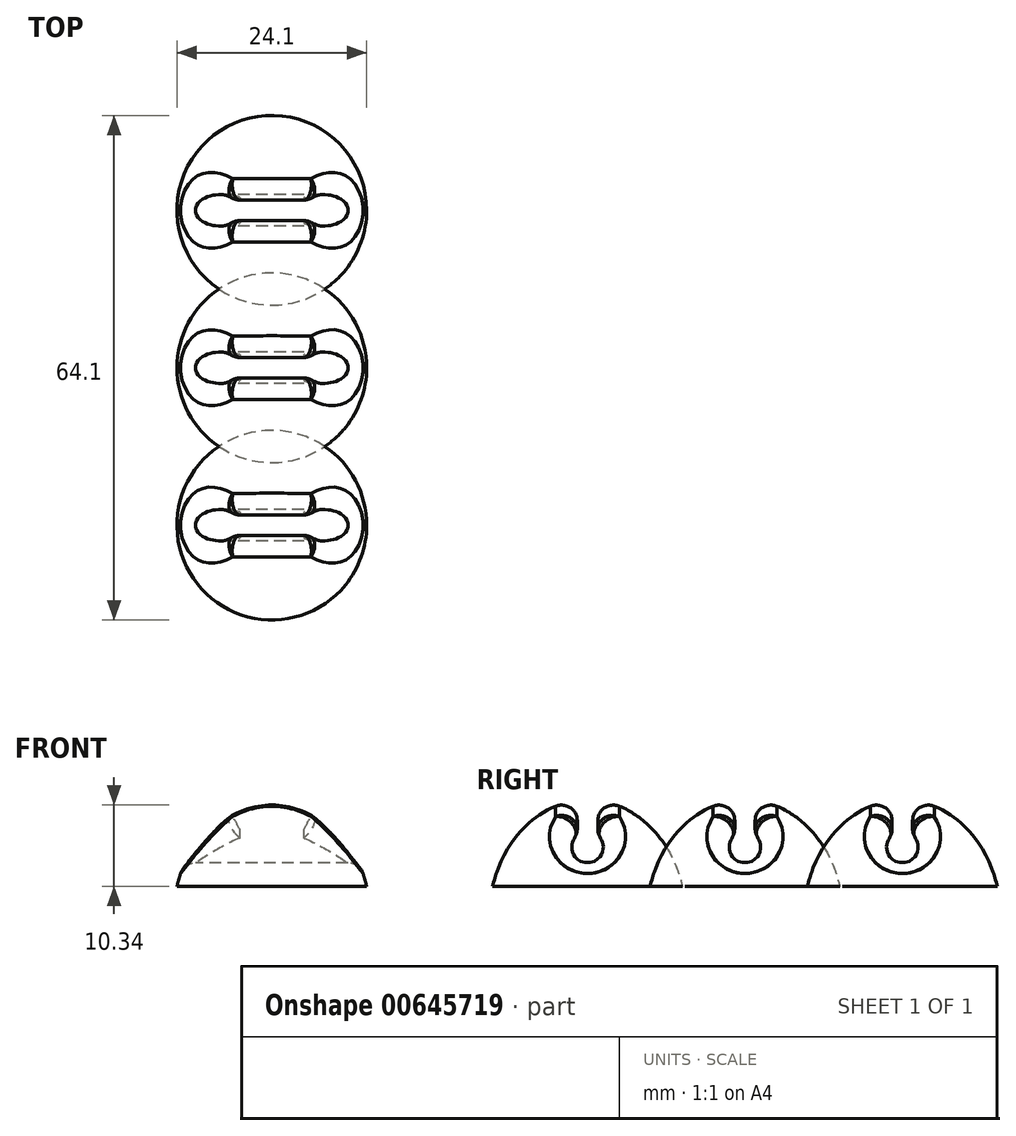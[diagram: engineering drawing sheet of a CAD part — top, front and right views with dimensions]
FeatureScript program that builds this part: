
annotation { "Feature Type Name" : "Feature", "Feature Type Description" : "" }
export const myFeature = defineFeature(function(context is Context, id is Id, definition is map)
    precondition{}
    {
        {
            var Q0;
            Q0=qCreatedBy(makeId("Right.planeOp"),FACE);
            var sketch = newSketch(context, id + "F0", { "sketchPlane" : qUnion([Q0])});
            skEllipse(sketch, "E0", {"center": v(0, -4) * mm, "majorRadius": 12.5 * mm, "minorRadius": 15 * mm, "majorAxis": v(1, 0)});
            skLineSegment(sketch, "E1.bottom", {"start": v(-40.37, 30.12) * mm, "end": v(0, 30.12) * mm});
            skLineSegment(sketch, "E1.top", {"start": v(-40.37, 0) * mm, "end": v(0, 0) * mm});
            skLineSegment(sketch, "E1.left", {"start": v(-40.37, 30.12) * mm, "end": v(-40.37, 0) * mm});
            skLineSegment(sketch, "E1.right", {"start": v(0, 30.12) * mm, "end": v(0, 0) * mm});
            skSolve(sketch);
        }
        {
            var Q0;
            {var subQ0=sQuery(id+"F0.wireOp",EDGE,"E1.top");var subQ1=sQuery(id+"F0.wireOp",EDGE,"E0");var subQ2=makeQuery(id+"F0.imprint","INTERSECT",VERTEX,{"derivedFrom":[subQ1,subQ0]});Q0=makeQuery(id+"F0.imprint","IMPRINT",FACE,{"disambiguationData":[TD([[makeQuery(id+"F0.imprint","IMPRINT",EDGE,{"disambiguationData":[TD([[subQ2,1.0]])],"derivedFrom":subQ1}),1.0]])]});}
            var Q1;
            Q1=sQuery(id+"F0.wireOp",EDGE,"E1.right");
            revolve(context, id + "F1", {"entities" : qUnion([Q0]), "axis" : qUnion([Q1]), "revolveType" : RevolveType.FULL});
        }
        {
            var Q0;
            Q0=qCreatedBy(makeId("Right.planeOp"),FACE);
            var sketch = newSketch(context, id + "F2", { "sketchPlane" : qUnion([Q0])});
            skArc(sketch, "E2", {"start": v(-1.3, 6.52) * mm, "mid": v(0, 3) * mm, "end": v(1.3, 6.52) * mm});
            skLineSegment(sketch, "E3.top", {"start": v(1.3, 24.85) * mm, "end": v(-1.3, 24.85) * mm});
            skLineSegment(sketch, "E3.left", {"start": v(1.3, 6.52) * mm, "end": v(1.3, 24.85) * mm});
            skLineSegment(sketch, "E3.right", {"start": v(-1.3, 6.52) * mm, "end": v(-1.3, 24.85) * mm});
            skPoint(sketch, "E3.middle", {"position": v(0, 15.36) * mm});
            skPoint(sketch, "E4.orphan", {"position": v(-1.3, 5.87) * mm});
            skPoint(sketch, "E5.orphan", {"position": v(1.3, 5.87) * mm});
            skSolve(sketch);
        }
        {
            var Q0;
            Q0=makeQuery(id+"F2.imprint","IMPRINT",FACE,{"disambiguationData":[TD([[makeQuery(id+"F2.imprint","IMPRINT",EDGE,{"derivedFrom":sQuery(id+"F2.wireOp",EDGE,"E2")}),1.0]])]});
            extrude(context, id + "F3", {"entities" : qUnion([Q0]), "depth" : 30 * mm, "offsetDistance" : 25 * mm, "hasSecondDirection" : true, "secondDirectionOppositeDirection" : true, "secondDirectionDepth" : 30 * mm});
        }
        {
            var Q0;
            Q0=makeQuery(id+"F3.opExtrude","SWEPT_EDGE",EDGE,{"disambiguationData":[OSD([sQuery(id+"F2.wireOp",EDGE,"E2"),sQuery(id+"F2.wireOp",EDGE,"E3.right")])]});
            var Q1;
            Q1=makeQuery(id+"F3.opExtrude","SWEPT_EDGE",EDGE,{"disambiguationData":[OSD([sQuery(id+"F2.wireOp",EDGE,"E2"),sQuery(id+"F2.wireOp",EDGE,"E3.left")])]});
            fillet(context, id + "F4", {"entities" : qUnion([Q0, Q1]), "radius" : 2 * mm, "tangentPropagation" : true, "allowEdgeOverflow" : false});
        }
        {
            var Q0;
            Q0=makeQuery(id+"F3.opExtrude","SWEPT_BODY",BODY,{"disambiguationData":[OSD([sQuery(id+"F2.wireOp",EDGE,"E2"),sQuery(id+"F2.wireOp",EDGE,"E3.top"),sQuery(id+"F2.wireOp",EDGE,"E3.left"),sQuery(id+"F2.wireOp",EDGE,"E3.right")])]});
            var Q1;
            Q1=makeQuery(id+"F1.opRevolve","SWEPT_BODY",BODY,{"disambiguationData":[OSD([sQuery(id+"F0.wireOp",EDGE,"E0"),sQuery(id+"F0.wireOp",EDGE,"E1.top"),sQuery(id+"F0.wireOp",EDGE,"E1.right")])]});
            booleanBodies(context, id + "F5", {"operationType" : BooleanOperationType.SUBTRACTION, "tools" : qUnion([Q0]), "targets" : qUnion([Q1])});
        }
        {
            var Q0;
            Q0=makeQuery(id+"F5.opBoolean","INTERSECT",EDGE,{"derivedFrom":[makeQuery(id+"F1.opRevolve","SWEPT_FACE",FACE,{"disambiguationData":[OSD([sQuery(id+"F0.wireOp",EDGE,"E0")])]}),makeQuery(id+"F3.opExtrude","SWEPT_FACE",FACE,{"disambiguationData":[OSD([sQuery(id+"F2.wireOp",EDGE,"E3.right")])]})]});
            fillet(context, id + "F6", {"entities" : qUnion([Q0]), "radius" : 2 * mm, "tangentPropagation" : true, "allowEdgeOverflow" : false});
        }
        {
            var Q0;
            Q0=makeQuery(id+"F1.opRevolve","SWEPT_BODY",BODY,{"disambiguationData":[OSD([sQuery(id+"F0.wireOp",EDGE,"E0"),sQuery(id+"F0.wireOp",EDGE,"E1.top"),sQuery(id+"F0.wireOp",EDGE,"E1.right")])]});
            transform(context, id + "F7", {"entities" : qUnion([Q0]), "transformType" : TransformType.TRANSLATION_3D, "dx" : 0 * mm, "dy" : 20 * mm, "dz" : 0 * mm, "makeCopy" : true});
        }
        {
            var Q0;
            Q0=makeQuery(id+"F7.opPattern","COPY",BODY,{"derivedFrom":makeQuery(id+"F1.opRevolve","SWEPT_BODY",BODY,{"disambiguationData":[OSD([sQuery(id+"F0.wireOp",EDGE,"E0"),sQuery(id+"F0.wireOp",EDGE,"E1.top"),sQuery(id+"F0.wireOp",EDGE,"E1.right")])]}),"instanceName":"1"});
            transform(context, id + "F8", {"entities" : qUnion([Q0]), "transformType" : TransformType.TRANSLATION_3D, "dx" : 0 * mm, "dy" : 20 * mm, "dz" : 0 * mm, "makeCopy" : true});
        }
    });
